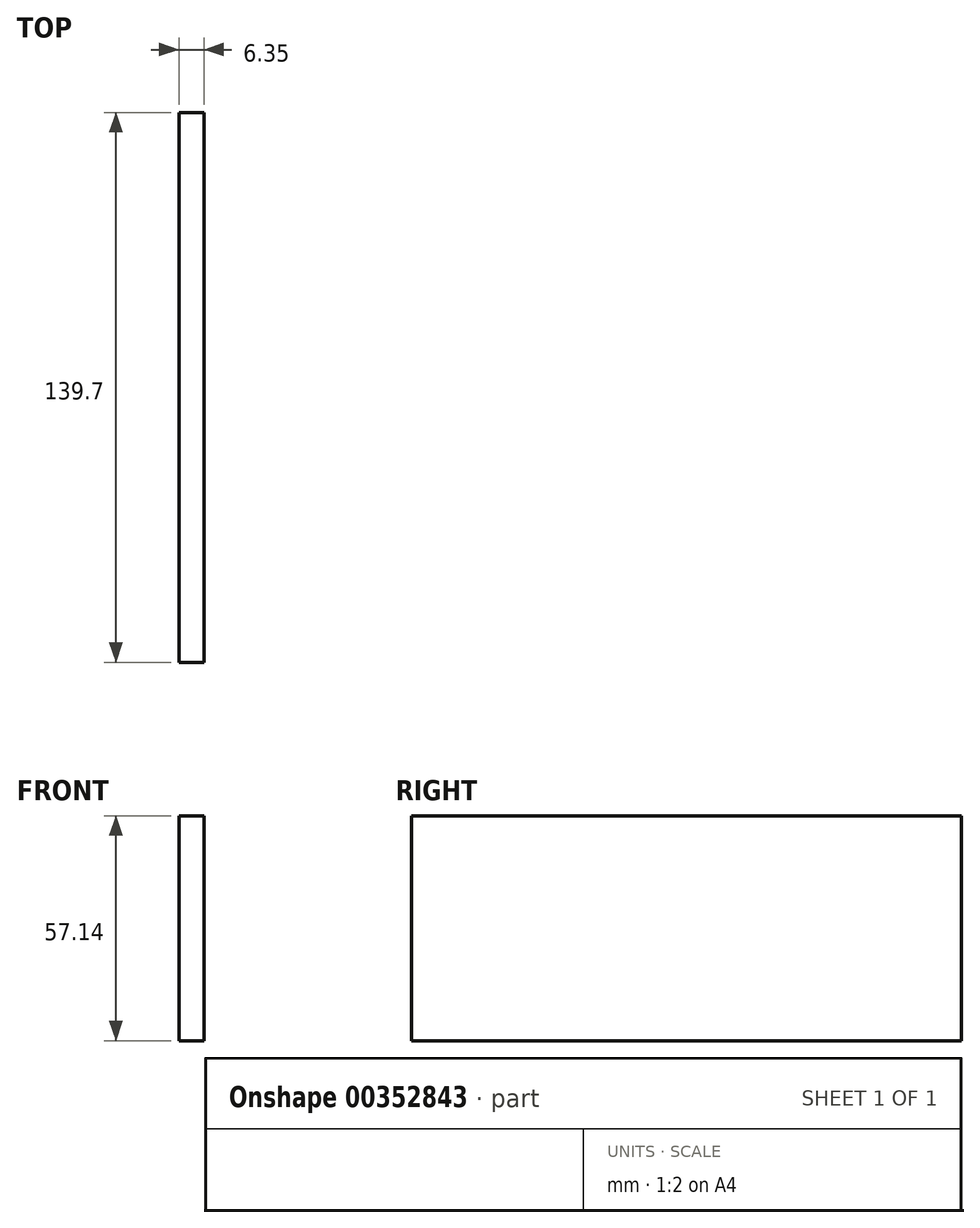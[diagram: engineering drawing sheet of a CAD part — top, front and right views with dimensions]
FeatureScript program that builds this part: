
annotation { "Feature Type Name" : "Feature", "Feature Type Description" : "" }
export const myFeature = defineFeature(function(context is Context, id is Id, definition is map)
    precondition{}
    {
        {
            var Q0;
            Q0=qCreatedBy(makeId("Right.planeOp"),FACE);
            var sketch = newSketch(context, id + "F0", { "sketchPlane" : qUnion([Q0])});
            skLineSegment(sketch, "E0.bottom", {"start": v(69.85, 28.58) * mm, "end": v(-69.85, 28.58) * mm});
            skLineSegment(sketch, "E0.top", {"start": v(69.85, -28.58) * mm, "end": v(-69.85, -28.58) * mm});
            skLineSegment(sketch, "E0.left", {"start": v(69.85, 28.58) * mm, "end": v(69.85, -28.58) * mm});
            skLineSegment(sketch, "E0.right", {"start": v(-69.85, 28.58) * mm, "end": v(-69.85, -28.58) * mm});
            skPoint(sketch, "E0.middle", {"position": v(0, 0) * mm});
            skSolve(sketch);
        }
        {
            var Q0;
            Q0 = qSketchRegion(id + "F0", true);
            extrude(context, id + "F1", {"entities" : qUnion([Q0]), "depth" : 6.35 * mm});
        }
    });
